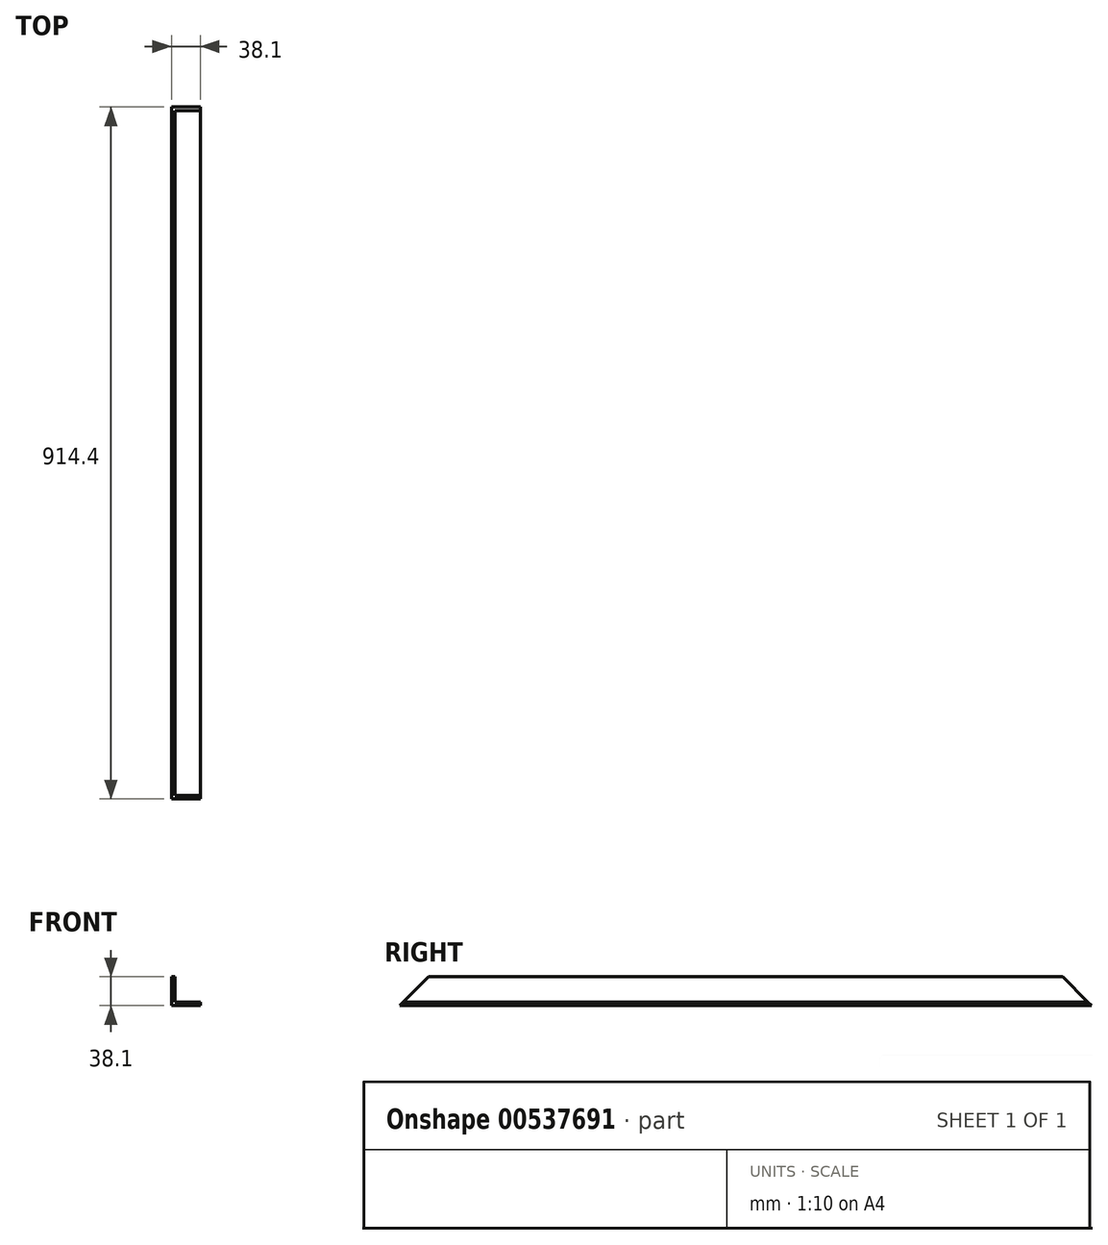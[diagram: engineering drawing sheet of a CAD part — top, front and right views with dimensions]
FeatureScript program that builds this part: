
annotation { "Feature Type Name" : "Feature", "Feature Type Description" : "" }
export const myFeature = defineFeature(function(context is Context, id is Id, definition is map)
    precondition{}
    {
        {
            var Q0;
            Q0=qCreatedBy(makeId("Front.planeOp"),FACE);
            var sketch = newSketch(context, id + "F0", { "sketchPlane" : qUnion([Q0])});
            skLineSegment(sketch, "E0", {"start": v(0, 0) * mm, "end": v(0, 38.1) * mm});
            skLineSegment(sketch, "E1", {"start": v(0, 38.1) * mm, "end": v(4.76, 38.1) * mm});
            skLineSegment(sketch, "E2", {"start": v(4.76, 38.1) * mm, "end": v(4.76, 4.76) * mm});
            skLineSegment(sketch, "E3", {"start": v(4.76, 4.76) * mm, "end": v(38.1, 4.76) * mm});
            skLineSegment(sketch, "E4", {"start": v(38.1, 4.76) * mm, "end": v(38.1, 0) * mm});
            skLineSegment(sketch, "E5", {"start": v(38.1, 0) * mm, "end": v(0, 0) * mm});
            skSolve(sketch);
        }
        {
            var Q0;
            Q0 = qSketchRegion(id + "F0", true);
            extrude(context, id + "F1", {"entities" : qUnion([Q0]), "oppositeDirection" : true, "depth" : 914.4 * mm, "offsetDistance" : 25.4 * mm});
        }
        {
            var Q0;
            Q0=makeQuery(id+"F1.opExtrude","SWEPT_FACE",FACE,{"disambiguationData":[OSD([sQuery(id+"F0.wireOp",EDGE,"E0")])]});
            var sketch = newSketch(context, id + "F2", { "sketchPlane" : qUnion([Q0])});
            skLineSegment(sketch, "E6.0", {"start": v(-914.4, 38.1) * mm, "end": v(0, 38.1) * mm});
            skLineSegment(sketch, "E6.1", {"start": v(-914.4, 0) * mm, "end": v(-914.4, 38.1) * mm});
            skLineSegment(sketch, "E6.2", {"start": v(0, 0) * mm, "end": v(0, 38.1) * mm});
            skLineSegment(sketch, "E7", {"start": v(0, 0) * mm, "end": v(-38.1, 38.1) * mm});
            skLineSegment(sketch, "E8", {"start": v(-914.4, 0) * mm, "end": v(-876.3, 38.1) * mm});
            skSolve(sketch);
        }
        {
            var Q0;
            Q0 = qSketchRegion(id + "F2", true);
            extrude(context, id + "F3", {"entities" : qUnion([Q0]), "operationType" : NewBodyOperationType.REMOVE, "endBound" : BoundingType.THROUGH_ALL, "oppositeDirection" : true, "depth" : 25.4 * mm, "offsetDistance" : 25.4 * mm});
        }
    });
